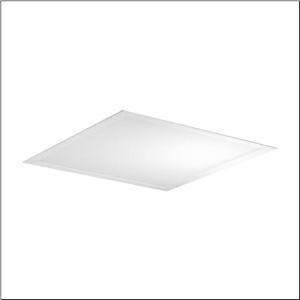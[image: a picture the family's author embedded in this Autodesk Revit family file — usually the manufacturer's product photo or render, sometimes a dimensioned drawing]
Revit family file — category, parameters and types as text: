
# Revit family: apollon_r__21_square_51mq11wd2m14_9a28
name_source: partatom
category: Lighting Fixtures
units: mm (PartAtom-declared; Revit-internal decimal feet)

## family parameters
Cut with Voids When Loaded = No
Host = Face
Light Source = No
Part Type = Normal
Room Calculation Point = No
Round Connector Dimension = Use Diameter
Shared = No

## types (1)
- --- (1 x LED, 4200 lm, 26 W, 4000K)
    Apparent Load = 26 VA
    CIE Flux Codes = 60 87 97 100 100
    Color Rendering = 80
    Color Temperature = 4000K
    Default Elevation = 1800 mm
    Description = Apollon® 21 square, office luminaire, primary optical cover: micro prismatic cover, of PMMA, CAT 2 (L<= 3000cd/m²), light emission: direct distribution, primary light characteristic: symmetric, installation type: lay-in mounting, LED, rated luminous flux: 4.200lm, luminous efficacy: 162lm/W, light colour: 830/840, colour temperature: 3000/4000K, with terminal, 5-pole, mains connection: 220..240V, AC/DC, 0/50..60Hz, rated input power: 26W, housing, of aluminium, coated, traffic white (RAL 9016), module: M625, length: 620mm, width: 620mm, height: 30mm, housing upper side, of sheet steel, galvanised, protection rating (complete): IP20, protection rating (lamp compartment, on room side): IP50, insulation class (complete): insulation class II (safety insulation), certification: CE, ENEC, impact resistance: IK03, permissible operating ambient temperature: -20..+45°C, permissible storage temperature: -40..+80°C, packaging unit: 1 piece
    Height = 0 mm  [stored 0 ft]
    Lamp = 1 x LED
    Lamp Light Flux = 4200 lm
    Lamp Power = 26 W
    Lamp count = 1
    Length = 620 mm
    Luminous efficacy = 162 lm/W
    Manufacturer = Siteco
    ModVariant = No
    Model = 51MQ11WD2M14
    Mounting Place = Ceiling
    Mounting Type = Recessed
    Number of Poles = 1
    OnlyDefault = Yes
    Power Factor = 1
    Product Name = Apollon® 21 square
    Product group = office luminaire | ceiling recessed
    ProductGroupID = 401
    Protection Class = Protection class II
    Protection Degree = IP 20
    RLX_Detail_Level = 1
    RLX_Emergency_Light_Flux = 0 lm
    RLX_Emergency_Type = 0
    RLX_Emergency_Type_DB = No
    RlxData = <blob elided: 13141 chars, md5=40b81b34>
    Socket = socket
    Standby Power = 0 W
    System Light Flux = 4200 lm
    System Power = 26 W
    Type Comments = factory setting
    Type Image = l_1291054.jpg
    URL = http://relux.com
    VarID = @adj_026999
    Voltage = 0 V
    Weight = 0.00 kg
    Width = 620 mm

note: [stored X ft] marks values corroborated as IEEE doubles in the binary element streams (Revit-internal decimal feet)

## geometry (parser evidence)
native form markers: Sweep x11
no freeform markers — native parametric forms only
